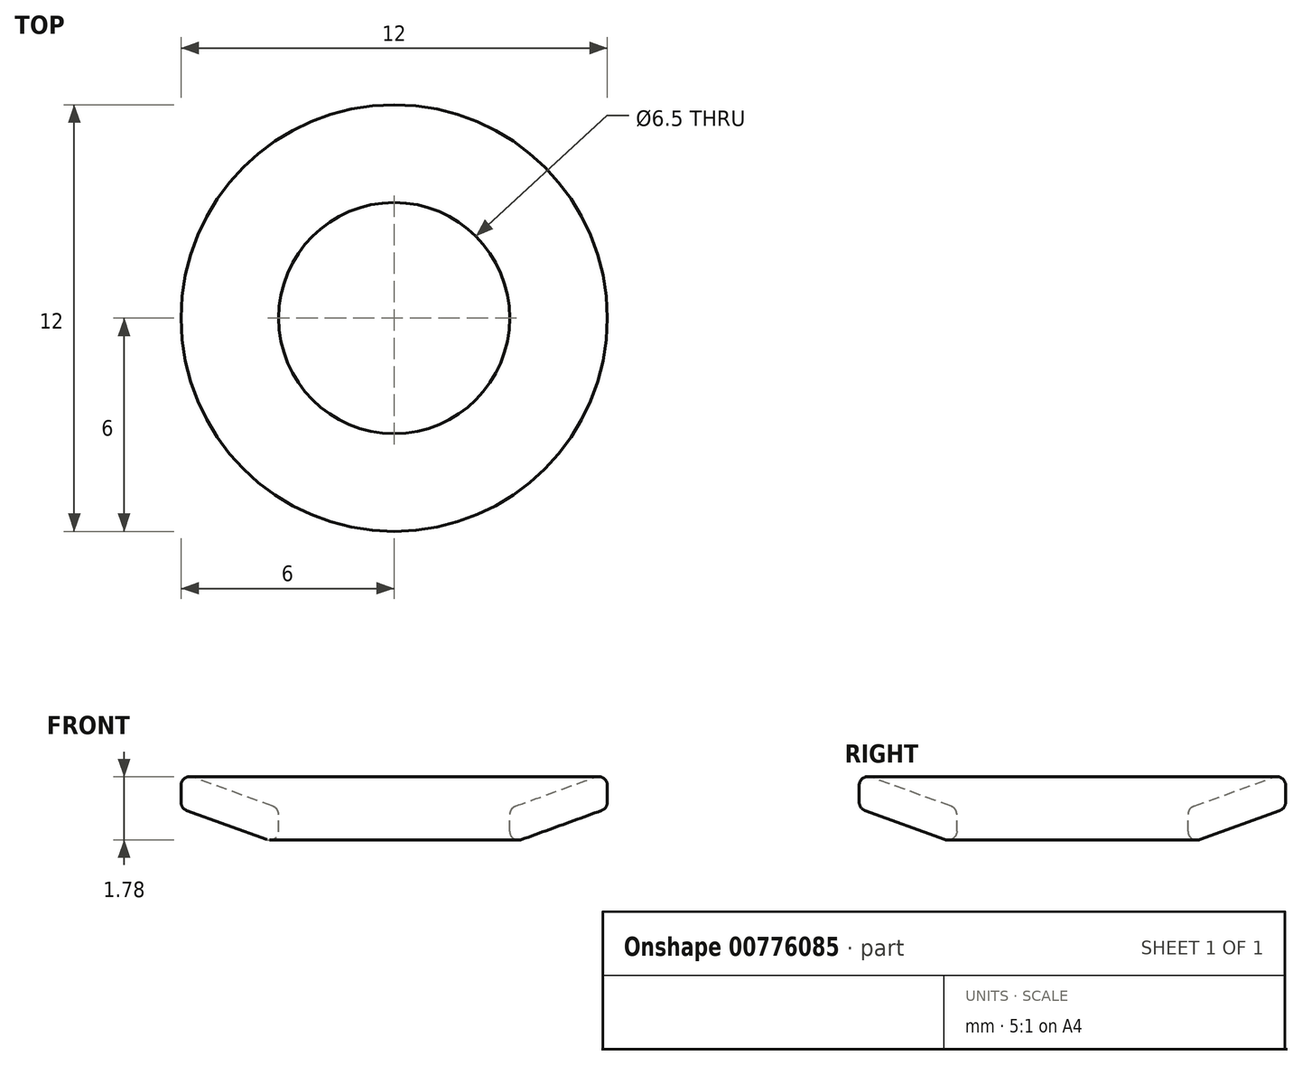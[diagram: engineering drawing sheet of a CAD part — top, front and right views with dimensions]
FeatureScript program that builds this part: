
annotation { "Feature Type Name" : "Feature", "Feature Type Description" : "" }
export const myFeature = defineFeature(function(context is Context, id is Id, definition is map)
    precondition{}
    {
        {
            var Q0;
            Q0=qCreatedBy(makeId("Right.planeOp"),FACE);
            var sketch = newSketch(context, id + "F0", { "sketchPlane" : qUnion([Q0])});
            skLineSegment(sketch, "E0.right", {"start": v(6, 1) * mm, "end": v(6, 2) * mm});
            skLineSegment(sketch, "E1", {"start": v(3.25, 0) * mm, "end": v(3.25, 1) * mm});
            skLineSegment(sketch, "E2", {"start": v(3.25, 0) * mm, "end": v(6, 1) * mm});
            skLineSegment(sketch, "E3", {"start": v(6, 2) * mm, "end": v(3.25, 1) * mm});
            skPoint(sketch, "E4.orphan", {"position": v(6, 0) * mm});
            skPoint(sketch, "E0.top.start.orphan", {"position": v(3.25, 2) * mm});
            skLineSegment(sketch, "E5", {"start": v(0, 0) * mm, "end": v(0, -3.64) * mm});
            skSolve(sketch);
        }
        {
            var Q0;
            Q0 = qSketchRegion(id + "F0", true);
            var Q1;
            Q1=sQuery(id+"F0.wireOp",EDGE,"E5");
            revolve(context, id + "F1", {"surfaceOperationType" : NewSurfaceOperationType.NEW, "entities" : qUnion([Q0]), "axis" : qUnion([Q1]), "revolveType" : RevolveType.FULL});
        }
        {
            var Q0;
            Q0=makeQuery(id+"F1.opRevolve","SWEPT_EDGE",EDGE,{"disambiguationData":[OSD([sQuery(id+"F0.wireOp",EDGE,"E1"),sQuery(id+"F0.wireOp",EDGE,"E2")])]});
            var Q1;
            Q1=makeQuery(id+"F1.opRevolve","SWEPT_EDGE",EDGE,{"disambiguationData":[OSD([sQuery(id+"F0.wireOp",EDGE,"E0.right"),sQuery(id+"F0.wireOp",EDGE,"E3")])]});
            var Q2;
            Q2=makeQuery(id+"F1.opRevolve","SWEPT_EDGE",EDGE,{"disambiguationData":[OSD([sQuery(id+"F0.wireOp",EDGE,"E1"),sQuery(id+"F0.wireOp",EDGE,"E3")])]});
            var Q3;
            Q3=makeQuery(id+"F1.opRevolve","SWEPT_EDGE",EDGE,{"disambiguationData":[OSD([sQuery(id+"F0.wireOp",EDGE,"E0.right"),sQuery(id+"F0.wireOp",EDGE,"E2")])]});
            fillet(context, id + "F2", {"entities" : qUnion([Q0, Q1, Q2, Q3]), "radius" : .25 * mm, "tangentPropagation" : true, "allowEdgeOverflow" : false});
        }
    });
